# Revit family: AP_Accessible 140 Degree Cont_BIM
name_source: partatom
category: Generic Models
units: mm (PartAtom-declared; Revit-internal decimal feet)

## family parameters
Always vertical = Yes
Can host rebar = No
Cut with Voids When Loaded = No
Maintain Annotation Orientation = No
OmniClass Number = 23.25.45.11.25.15
Part Type = Normal
Room Calculation Point = No
Round Connector Dimension = Use Diameter
Shared = No
Work Plane-Based = No

## types (1)
- Aliro - Accessible 140° Continuous Grab Rail
    Brass-SKU = 14736
    Copper-SKU = 14737
    Default Elevation = 0 mm  [stored 0 ft]
    Description = Aliro - Accessible 140° Continuous Grab Rail
    Gunmetal-SKU = 14738
    Manufacturer = ABI Interiors Pty Ltd
    StainlessSteel-SKU = 14739
    URL-AU InfoSheet = https://abi.guide

note: [stored X ft] marks values corroborated as IEEE doubles in the binary element streams (Revit-internal decimal feet)

## geometry (parser evidence)
native form markers: Sweep x3
no freeform markers — native parametric forms only
